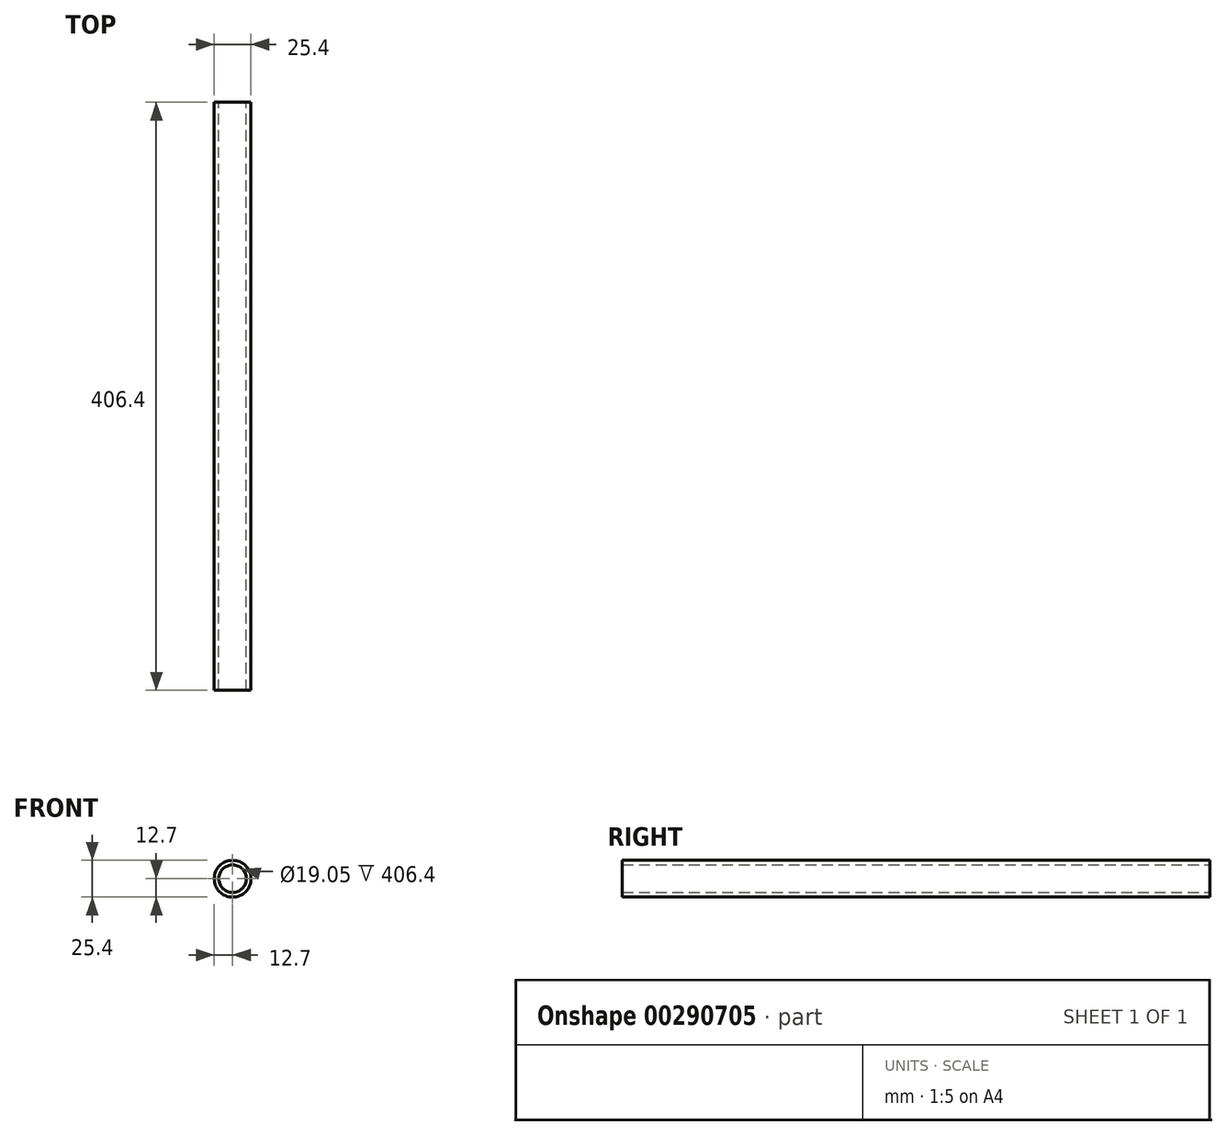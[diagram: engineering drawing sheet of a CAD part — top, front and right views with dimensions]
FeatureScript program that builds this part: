
annotation { "Feature Type Name" : "Feature", "Feature Type Description" : "" }
export const myFeature = defineFeature(function(context is Context, id is Id, definition is map)
    precondition{}
    {
        {
            var Q0;
            Q0=qCreatedBy(makeId("Front.planeOp"),FACE);
            var sketch = newSketch(context, id + "F0", { "sketchPlane" : qUnion([Q0])});
            skCircle(sketch, "E0", {"center": v(0, 0) * mm, "radius": 12.7 * mm});
            skCircle(sketch, "E1.0", {"center": v(0, 0) * mm, "radius": 9.53 * mm});
            skSolve(sketch);
        }
        {
            var Q0;
            Q0=makeQuery(id+"F0.imprint","IMPRINT",FACE,{"disambiguationData":[TD([[makeQuery(id+"F0.imprint","IMPRINT",EDGE,{"derivedFrom":sQuery(id+"F0.wireOp",EDGE,"E0")}),1.0]])]});
            extrude(context, id + "F1", {"entities" : qUnion([Q0]), "depth" : 406.4 * mm});
        }
    });
